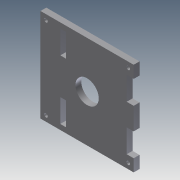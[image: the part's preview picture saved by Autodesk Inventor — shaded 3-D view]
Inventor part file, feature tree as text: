
AUTODESK INVENTOR PART (.ipt)
format: ipt  version: 2011 (Build 150239000, 239)  size: 342,528 bytes
history: native  units: in
note: dims shown in document units (in); Inventor stores cm internally (conversion verified against a paired STEP export)
features: extrude x16, sketch x16
ambient origin geometry x8: Origin, YZ Plane, XZ Plane, XY Plane, X Axis, Y Axis, Z Axis, Center Point
bodies: Solid1 (feature_tree)
feature tree (32):
  extrude  "Extrusion1"  Depth=4.05in
  extrude  "Extrusion2"  Depth=2.05in
  extrude  "Extrusion3"  Depth=1.7in
  extrude  "Extrusion4"  Depth=1.0in
  extrude  "Extrusion5"  Depth=1.75in
  extrude  "Extrusion6"  Depth=1.0in
  extrude  "Extrusion7"  Depth=1.0in
  extrude  "Extrusion8"  Depth=1.0in
  extrude  "Extrusion9"  Depth=1.0in
  extrude  "Extrusion10"  Depth=1.0in
  extrude  "Extrusion11"  Depth=1.0in
  extrude  "Extrusion12"  Depth=0.2345in
  extrude  "Extrusion13"  Depth=0.2345in
  extrude  "Extrusion14"  Depth=4.0in
  extrude  "Extrusion15"  Depth=0.156in
  extrude  "Extrusion16"  Depth=0.5in
  sketch  "Sketch1"  dims[d0=4.0in d1=4.05in]
  sketch  "Sketch2"  dims[d2=2.0in d3=2.05in]
  sketch  "Sketch3"  dims[d4=0.9in d5=1.7in]
  sketch  "Sketch4"  dims[d6=1.8in d7=1.0in]
  sketch  "Sketch5"  dims[d8=0.3in d9=1.75in]
  sketch  "Sketch6"  dims[d10=0.25in d11=1.0in]
  sketch  "Sketch7"  dims[d12=0.25in d13=1.0in]
  sketch  "Sketch8"  dims[d14=1.275in d15=1.0in]
  sketch  "Sketch9"  dims[d16=0.25in d17=1.0in]
  sketch  "Sketch11"  dims[d18=0.275in d19=1.0in]
  sketch  "Sketch12"  dims[d20=0.25in d21=0.0in d22=1.0in]
  sketch  "Sketch13"  dims[d23=0.25in d24=0.0in d25=0.2345in]
  sketch  "Sketch14"  dims[d26=0.2345in d27=0.2345in]
  sketch  "Sketch15"  dims[d28=0.2345in d29=4.0in]
  sketch  "Sketch16"  dims[d30=0.156in d31=0.156in]
  sketch  "Sketch17"  dims[d32=0.25in d33=0.0in d34=0.5in d35=0.5in d36=0.25in d37=0.0in d38=4.0in d39=0.2345in d40=0.2345in d41=4.0in d42=0.5in d43=0.3in d44=0.2in d45=0.25in d46=0.0in d47=0.3in d48=0.25in d49=0.0in d50=4.0in d51=0.2345in d52=4.0in d53=0.2345in d54=0.2345in d55=0.2345in d56=0.156in d57=0.156in d58=0.25in d59=0.0in d60=4.0in d61=0.25in d62=0.0in d63=0.25in d64=0.0in d67=1.0in d68=1.0in d69=0.3in d70=0.25in d71=0.0in d72=0.25in d73=0.0in d74=0.25in d75=0.0in d76=0.25in d77=0.0in d78=0.025in d79=0.025in d80=0.25in d81=0.0in d82=2.0in d83=1.7655in d84=0.156in d85=0.156in d86=0.156in d87=0.156in d88=0.25in d89=0.0in d90=1.0in d91=1.0in d92=0.0in]
